# Revit family: Shower-Whitehall-BestCare-WH538-WHCSH-WHCHS
name_source: partatom
category: Plumbing Fixtures
units: mm (PartAtom-declared; Revit-internal decimal feet)

## family parameters
Cut with Voids When Loaded = No
Host = Face
OmniClass Number = 23.45.05.14.17
OmniClass Title = Showers
Part Type = Normal
Room Calculation Point = No
Round Connector Dimension = Use Diameter
Shared = Yes

## types (1)
- WH538-WHCSH-WHCHS
    ADA Compliant = Yes
    Assembly Code = D2010710
    CW Connection = Yes
    CWFU = 3
    Cold Water Connection Diameter = 1/2"
    Cold Water Connection Radius = 1/4"
    Default Elevation = 72"
    Description = BestCare® Ligature-Resistant Built-in Shower with Semi-Permanent Collapsible Handheld Shower
    Escutcheon Plate Width = 5 1/8"
    Flow Rate = 1.5 GPM
    HW Connection = Yes
    HWFU = 3
    Handheld Shower Material = Stainless Steel-Whitehall-Satin
    Hot Water Connection Diameter = 1/2"
    Hot Water Connection Radius = 1/4"
    IAPMO Compliance = UPC, California Building Code -Title 24, Federal Public Law 111-380 - No Lead
    Installation Type = Wall Mounted
    Manufacturer = Whitehall Mfg.
    Maximum Operating Pressure = 125 PSI (862 kPa)
    Model = WH538-WHCSH-WHCHS
    Product Documentation Link = https://www.whitehallmfg.com
    Product Page URL = https://www.whitehallmfg.com
    Showerhead Material = Brass-Whitehall-Chrome Plated
    Support Material = Stainless Steel-Whitehall-Powder Coated
    Temperature Range = 85°F-115°F (29°C-46°C)
    Tempered Water Connection = Yes
    Tempered Water Connection Diameter = 1/2"
    Tri-Lever Handle Diameter = 5 1/2"
    Tri-Lever Handle Material = Brass-Whitehall-Chrome Plated
    URL = https://www.whitehallmfg.com
    Vent Connection = No
    WFU = 0
    WHCHS Series Handheld Shower Height = 34"
    WHCHS Series Handheld Shower Width = 8"
    WHCSH Conical Shower Head Height = 72"
    WHCSH Conical Shower Head Width = 8"
    WHDIV Diverter Valve with Tri-Lever Handle Height = 34"
    WHDIV Diverter Valve with Tri-Lever Handle Width = 21"
    WHSV16 Control Valve Mixing Valve with Tri-Lever Handle Height = 34"
    WHSV16 Control Valve Mixing Valve with Tri-Lever Handle Width = 28"
    Waste Connection = No

## geometry (parser evidence)
native form markers: Sweep x16
no freeform markers — native parametric forms only
